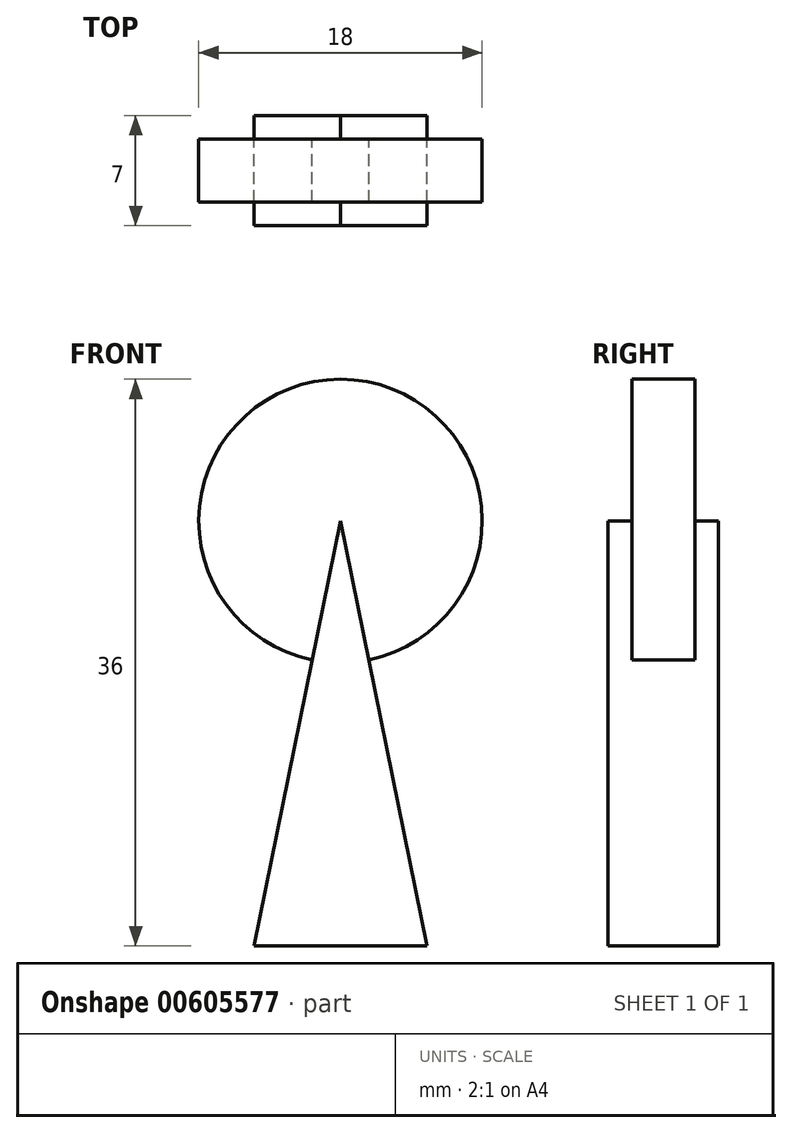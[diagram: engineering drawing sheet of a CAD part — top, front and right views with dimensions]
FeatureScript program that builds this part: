
annotation { "Feature Type Name" : "Feature", "Feature Type Description" : "" }
export const myFeature = defineFeature(function(context is Context, id is Id, definition is map)
    precondition{}
    {
        {
            var Q0;
            Q0=qCreatedBy(makeId("Front.planeOp"),FACE);
            var sketch = newSketch(context, id + "F0", { "sketchPlane" : qUnion([Q0])});
            skCircle(sketch, "E0", {"center": v(0, 27) * mm, "radius": 9 * mm});
            skLineSegment(sketch, "E1", {"start": v(0, 36) * mm, "end": v(0, 0) * mm});
            skSolve(sketch);
        }
        {
            var Q0;
            {var subQ0=sQuery(id+"F0.wireOp",EDGE,"E1");var subQ1=sQuery(id+"F0.wireOp",EDGE,"E0");var subQ2=makeQuery(id+"F0.imprint","INTERSECT",VERTEX,{"disambiguationData":[OD(0.0)],"derivedFrom":[subQ1,subQ0]});Q0=makeQuery(id+"F0.imprint","IMPRINT",FACE,{"disambiguationData":[TD([[makeQuery(id+"F0.imprint","IMPRINT",EDGE,{"disambiguationData":[TD([[subQ2,1.0]])],"derivedFrom":subQ1}),1.0]])]});}
            var Q1;
            {var subQ0=sQuery(id+"F0.wireOp",EDGE,"E1");var subQ1=sQuery(id+"F0.wireOp",EDGE,"E0");var subQ2=makeQuery(id+"F0.imprint","INTERSECT",VERTEX,{"disambiguationData":[OD(0.0)],"derivedFrom":[subQ1,subQ0]});Q1=makeQuery(id+"F0.imprint","IMPRINT",FACE,{"disambiguationData":[TD([[makeQuery(id+"F0.imprint","IMPRINT",EDGE,{"disambiguationData":[TD([[subQ2,-1.0]])],"derivedFrom":subQ1}),1.0]])]});}
            extrude(context, id + "F1", {"entities" : qUnion([Q0, Q1]), "endBound" : BoundingType.SYMMETRIC, "depth" : 4 * mm, "offsetDistance" : 25.4 * mm});
        }
        {
            var Q0;
            Q0=qCreatedBy(makeId("Front.planeOp"),FACE);
            var sketch = newSketch(context, id + "F2", { "sketchPlane" : qUnion([Q0])});
            skLineSegment(sketch, "E2", {"start": v(0, 27) * mm, "end": v(-5.5, 0) * mm});
            skLineSegment(sketch, "E3", {"start": v(-5.5, 0) * mm, "end": v(5.5, 0) * mm});
            skLineSegment(sketch, "E4", {"start": v(5.5, 0) * mm, "end": v(0, 27) * mm});
            skSolve(sketch);
        }
        {
            var Q0;
            Q0=qSketchRegion(id+"F2",true);
            extrude(context, id + "F3", {"entities" : qUnion([Q0]), "operationType" : NewBodyOperationType.ADD, "endBound" : BoundingType.SYMMETRIC, "depth" : 7 * mm, "offsetDistance" : 25 * mm});
        }
        {
            var Q0;
            Q0=makeQuery(id+"F1.opExtrude","SWEPT_BODY",BODY,{"disambiguationData":[OSD([sQuery(id+"F0.wireOp",EDGE,"E0")])]});
            var Q1;
            Q1=qCreatedBy(makeId("Front.planeOp"),FACE);
            mirror(context, id + "F4", {"operationType" : NewBodyOperationType.ADD, "entities" : qUnion([Q0]), "mirrorPlane" : qUnion([Q1])});
        }
    });
